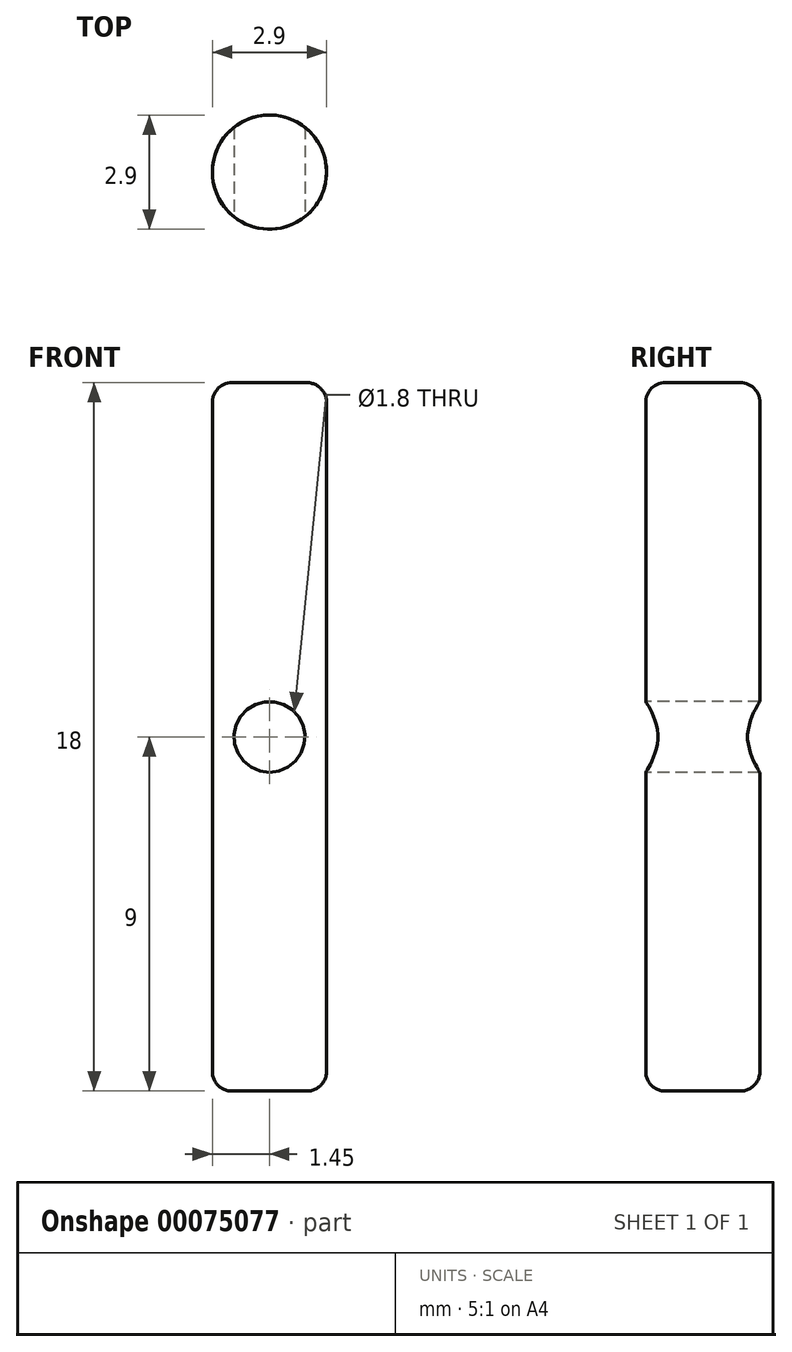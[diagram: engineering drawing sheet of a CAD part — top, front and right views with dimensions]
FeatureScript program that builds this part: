
annotation { "Feature Type Name" : "Feature", "Feature Type Description" : "" }
export const myFeature = defineFeature(function(context is Context, id is Id, definition is map)
    precondition{}
    {
        {
            var Q0;
            Q0=qCreatedBy(makeId("Top.planeOp"),FACE);
            var sketch = newSketch(context, id + "F0", { "sketchPlane" : qUnion([Q0])});
            skCircle(sketch, "E0", {"center": v(0, 0) * mm, "radius": 1.45 * mm});
            skSolve(sketch);
        }
        {
            var Q0;
            Q0=makeQuery(id+"F0.imprint","IMPRINT",FACE,{"disambiguationData":[TD([[makeQuery(id+"F0.imprint","IMPRINT",EDGE,{"derivedFrom":sQuery(id+"F0.wireOp",EDGE,"E0")}),1.0]])]});
            extrude(context, id + "F1", {"entities" : qUnion([Q0]), "endBound" : BoundingType.SYMMETRIC, "depth" : 18 * mm});
        }
        {
            var Q0;
            Q0=qCreatedBy(makeId("Front.planeOp"),FACE);
            var sketch = newSketch(context, id + "F2", { "sketchPlane" : qUnion([Q0])});
            skCircle(sketch, "E1", {"center": v(0, 0) * mm, "radius": 0.9 * mm});
            skSolve(sketch);
        }
        {
            var Q0;
            Q0=makeQuery(id+"F2.imprint","IMPRINT",FACE,{"disambiguationData":[TD([[makeQuery(id+"F2.imprint","IMPRINT",EDGE,{"derivedFrom":sQuery(id+"F2.wireOp",EDGE,"E1")}),1.0]])]});
            extrude(context, id + "F3", {"entities" : qUnion([Q0]), "operationType" : NewBodyOperationType.REMOVE, "endBound" : BoundingType.SYMMETRIC, "oppositeDirection" : true, "depth" : 25 * mm});
        }
        {
            var Q0;
            Q0=makeQuery(id+"F1.opExtrude","CAP_EDGE",EDGE,{"disambiguationData":[OSD([sQuery(id+"F0.wireOp",EDGE,"E0")])],"isStart":false});
            var Q1;
            Q1=makeQuery(id+"F1.opExtrude","CAP_EDGE",EDGE,{"disambiguationData":[OSD([sQuery(id+"F0.wireOp",EDGE,"E0")])],"isStart":true});
            fillet(context, id + "F4", {"entities" : qUnion([Q0, Q1]), "radius" : .5 * mm, "tangentPropagation" : true, "allowEdgeOverflow" : false});
        }
    });
